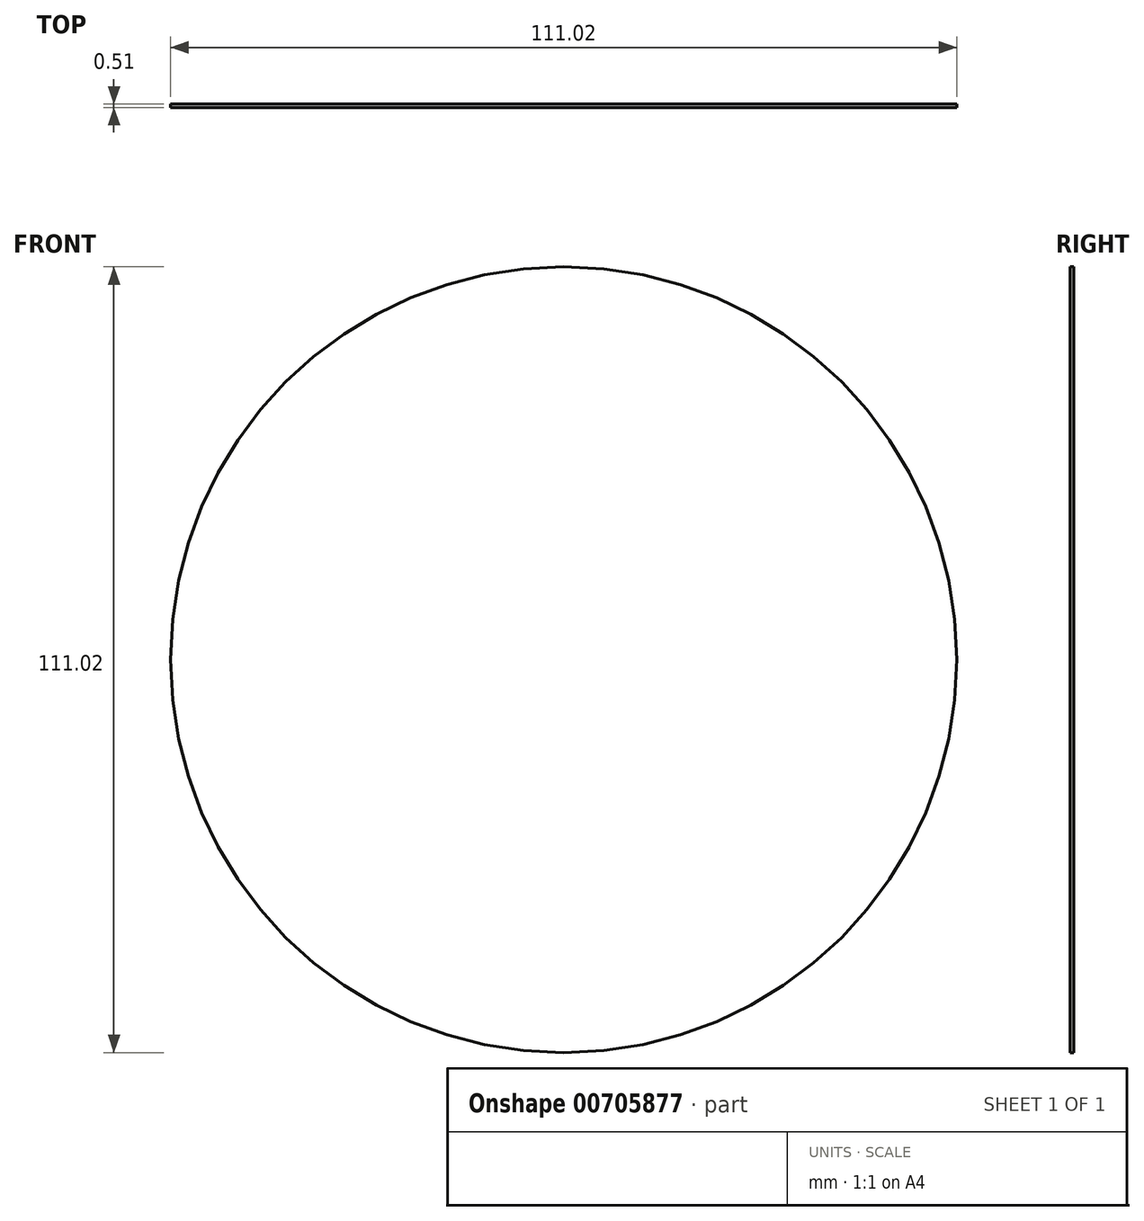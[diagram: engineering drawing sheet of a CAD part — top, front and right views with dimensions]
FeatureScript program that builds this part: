
annotation { "Feature Type Name" : "Feature", "Feature Type Description" : "" }
export const myFeature = defineFeature(function(context is Context, id is Id, definition is map)
    precondition{}
    {
        {
            var Q0;
            Q0=qCreatedBy(makeId("Front.planeOp"),FACE);
            var sketch = newSketch(context, id + "F0", { "sketchPlane" : qUnion([Q0])});
            skCircle(sketch, "E0", {"center": v(0, 0) * mm, "radius": 55.5 * mm});
            skSolve(sketch);
        }
        {
            var Q0;
            Q0=makeQuery(id+"F0.imprint","IMPRINT",FACE,{"disambiguationData":[TD([[makeQuery(id+"F0.imprint","IMPRINT",EDGE,{"derivedFrom":sQuery(id+"F0.wireOp",EDGE,"E0")}),1.0]])]});
            extrude(context, id + "F1", {"entities" : qUnion([Q0]), "depth" : 0.5 * mm, "offsetDistance" : 25.4 * mm});
        }
    });
